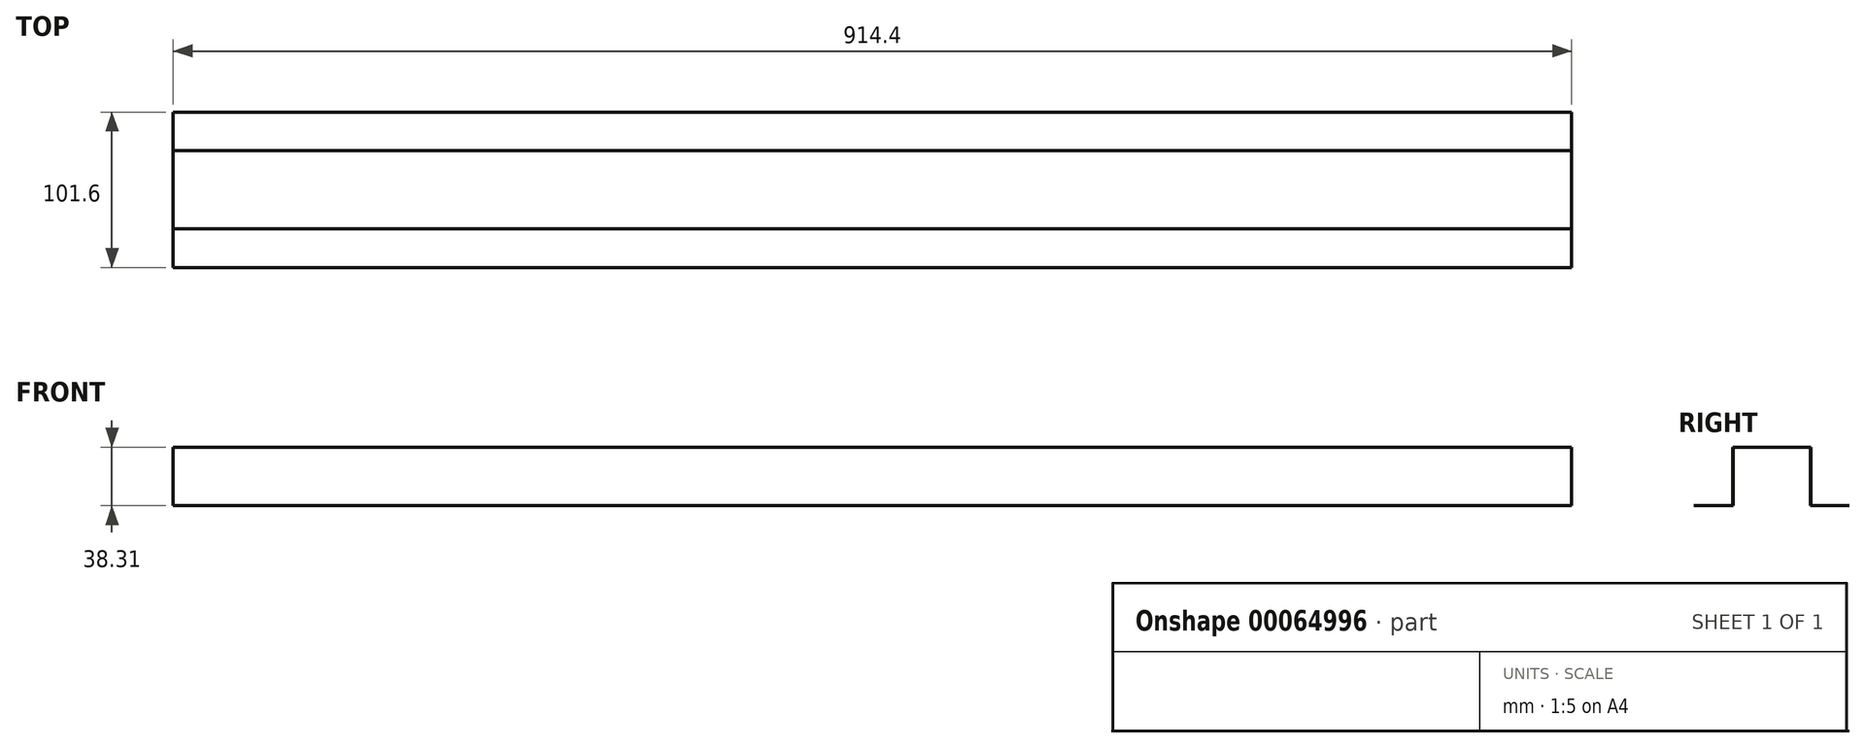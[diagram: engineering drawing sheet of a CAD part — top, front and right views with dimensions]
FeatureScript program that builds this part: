
annotation { "Feature Type Name" : "Feature", "Feature Type Description" : "" }
export const myFeature = defineFeature(function(context is Context, id is Id, definition is map)
    precondition{}
    {
        {
            var Q0;
            Q0=qCreatedBy(makeId("Right.planeOp"),FACE);
            var sketch = newSketch(context, id + "F0", { "sketchPlane" : qUnion([Q0])});
            skLineSegment(sketch, "E0", {"start": v(0, 3.5) * mm, "end": v(0, -1.39) * mm, "construction": true});
            skLineSegment(sketch, "E1", {"start": v(-50.8, 0.36) * mm, "end": v(-25.4, 0.36) * mm, "construction": true});
            skLineSegment(sketch, "E2", {"start": v(-25.4, 0.36) * mm, "end": v(-25.4, 38.46) * mm, "construction": true});
            skLineSegment(sketch, "E3", {"start": v(-25.4, 38.46) * mm, "end": v(0, 38.46) * mm, "construction": true});
            skLineSegment(sketch, "E4.MirrorCS", {"start": v(50.8, 0.36) * mm, "end": v(25.4, 0.36) * mm, "construction": true});
            skLineSegment(sketch, "E5.MirrorCS", {"start": v(25.4, 0.36) * mm, "end": v(25.4, 38.46) * mm, "construction": true});
            skLineSegment(sketch, "E6.MirrorCS", {"start": v(25.4, 38.46) * mm, "end": v(0, 38.46) * mm, "construction": true});
            skLineSegment(sketch, "E7.0", {"start": v(50.8, 0.46) * mm, "end": v(25.5, 0.46) * mm});
            skLineSegment(sketch, "E7.1", {"start": v(25.5, 0.46) * mm, "end": v(25.5, 38.56) * mm});
            skLineSegment(sketch, "E7.2", {"start": v(-50.8, 0.46) * mm, "end": v(-25.5, 0.46) * mm});
            skLineSegment(sketch, "E7.3", {"start": v(-25.5, 0.46) * mm, "end": v(-25.5, 38.56) * mm});
            skLineSegment(sketch, "E7.4", {"start": v(-25.5, 38.56) * mm, "end": v(0, 38.56) * mm});
            skLineSegment(sketch, "E7.5", {"start": v(25.5, 38.56) * mm, "end": v(0, 38.56) * mm});
            skLineSegment(sketch, "E8.0", {"start": v(50.8, 0.25) * mm, "end": v(25.5, 0.25) * mm});
            skLineSegment(sketch, "E9.0", {"start": v(-50.8, 0.25) * mm, "end": v(-25.3, 0.25) * mm});
            skLineSegment(sketch, "E9.1", {"start": v(-25.3, 0.25) * mm, "end": v(-25.3, 38.35) * mm});
            skLineSegment(sketch, "E9.2", {"start": v(50.8, 0.25) * mm, "end": v(25.3, 0.25) * mm});
            skLineSegment(sketch, "E9.3", {"start": v(25.3, 0.25) * mm, "end": v(25.3, 38.35) * mm});
            skLineSegment(sketch, "E9.4", {"start": v(25.3, 38.35) * mm, "end": v(0, 38.35) * mm});
            skLineSegment(sketch, "E9.5", {"start": v(-25.3, 38.35) * mm, "end": v(0, 38.35) * mm});
            skLineSegment(sketch, "E10", {"start": v(50.8, 0.46) * mm, "end": v(50.8, 0.25) * mm});
            skLineSegment(sketch, "E11", {"start": v(-50.8, 0.46) * mm, "end": v(-50.8, 0.25) * mm});
            skSolve(sketch);
        }
        {
            var Q0;
            Q0 = qSketchRegion(id + "F0", true);
            extrude(context, id + "F1", {"entities" : qUnion([Q0]), "endBound" : BoundingType.SYMMETRIC, "depth" : 914.4 * mm});
        }
    });
